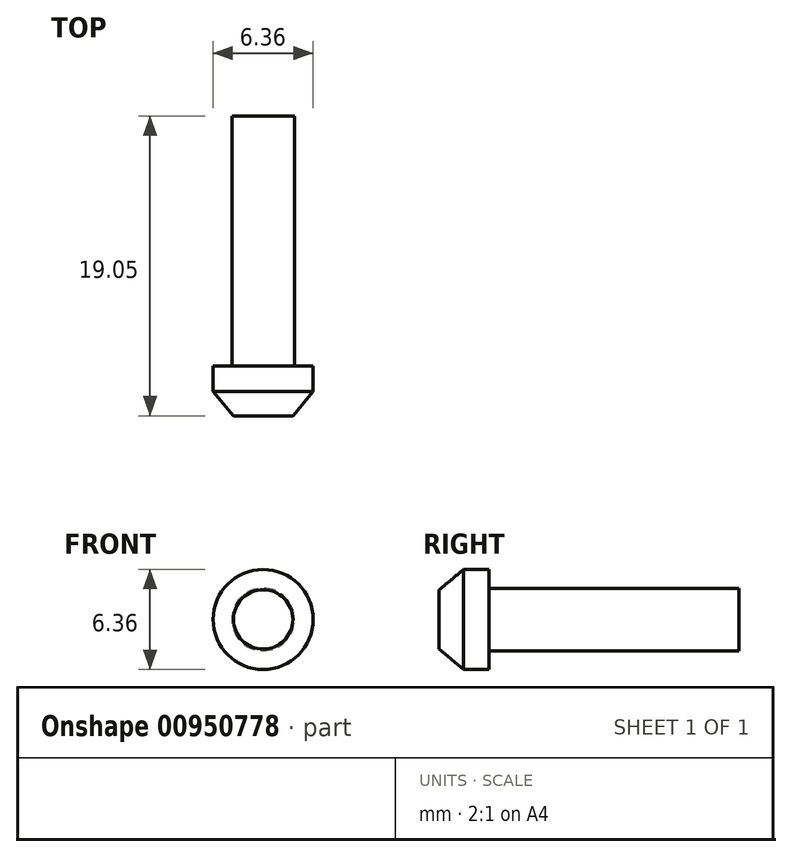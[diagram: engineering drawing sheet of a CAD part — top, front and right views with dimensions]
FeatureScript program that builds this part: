
annotation { "Feature Type Name" : "Feature", "Feature Type Description" : "" }
export const myFeature = defineFeature(function(context is Context, id is Id, definition is map)
    precondition{}
    {
        {
            var Q0;
            Q0=qCreatedBy(makeId("Front.planeOp"),FACE);
            var sketch = newSketch(context, id + "F0", { "sketchPlane" : qUnion([Q0])});
            skLineSegment(sketch, "E0", {"start": v(0, 0) * mm, "end": v(-1.98, 0) * mm});
            skCircle(sketch, "E1", {"center": v(0, 0) * mm, "radius": 1.98 * mm});
            skSolve(sketch);
        }
        {
            var Q0;
            Q0=makeQuery(id+"F0.imprint","IMPRINT",FACE,{"disambiguationData":[TD([[makeQuery(id+"F0.imprint","IMPRINT",EDGE,{"derivedFrom":sQuery(id+"F0.wireOp",EDGE,"E1")}),1.0]])]});
            extrude(context, id + "F1", {"entities" : qUnion([Q0]), "depth" : 15.88 * mm, "offsetDistance" : 25.4 * mm});
        }
        {
            var Q0;
            Q0=makeQuery(id+"F1.opExtrude","CAP_FACE",FACE,{"disambiguationData":[OSD([sQuery(id+"F0.wireOp",EDGE,"E1")])],"isStart":false});
            var sketch = newSketch(context, id + "F2", { "sketchPlane" : qUnion([Q0])});
            skLineSegment(sketch, "E2", {"start": v(0, 0) * mm, "end": v(-3.17, 0) * mm});
            skCircle(sketch, "E3", {"center": v(0, 0) * mm, "radius": 3.17 * mm});
            skSolve(sketch);
        }
        {
            var Q0;
            Q0=makeQuery(id+"F2.imprint","IMPRINT",FACE,{"disambiguationData":[TD([[makeQuery(id+"F2.imprint","IMPRINT",EDGE,{"derivedFrom":sQuery(id+"F2.wireOp",EDGE,"E3")}),1.0]])]});
            var Q1;
            Q1=makeQuery(id+"F2.imprint","IMPRINT",FACE,{"disambiguationData":[TD([[makeQuery(id+"F2.imprint","IMPRINT",EDGE,{"derivedFrom":makeQuery(id+"F1.opExtrude","CAP_EDGE",EDGE,{"disambiguationData":[OSD([sQuery(id+"F0.wireOp",EDGE,"E1")])],"isStart":false})}),1.0]])]});
            extrude(context, id + "F3", {"entities" : qUnion([Q0, Q1]), "operationType" : NewBodyOperationType.ADD, "depth" : 3.17 * mm, "offsetDistance" : 25.4 * mm});
        }
        {
            var Q0;
            Q0=qCreatedBy(makeId("Right.planeOp"),FACE);
            var sketch = newSketch(context, id + "F4", { "sketchPlane" : qUnion([Q0])});
            skLineSegment(sketch, "E4", {"start": v(-16.68, 3.85) * mm, "end": v(-19.86, 1.21) * mm});
            skLineSegment(sketch, "E5", {"start": v(-19.86, 1.21) * mm, "end": v(-19.86, 3.8) * mm});
            skLineSegment(sketch, "E6", {"start": v(-19.86, 3.8) * mm, "end": v(-16.68, 3.85) * mm});
            skLineSegment(sketch, "E7", {"start": v(0, 0) * mm, "end": v(-24.15, 0) * mm});
            skSolve(sketch);
        }
        {
            var Q0;
            Q0=makeQuery(id+"F4.imprint","IMPRINT",FACE,{"disambiguationData":[TD([[makeQuery(id+"F4.imprint","IMPRINT",EDGE,{"derivedFrom":sQuery(id+"F4.wireOp",EDGE,"E4")}),-1.0]])]});
            var Q1;
            Q1=sQuery(id+"F4.wireOp",EDGE,"E7");
            revolve(context, id + "F5", {"operationType" : NewBodyOperationType.REMOVE, "surfaceOperationType" : NewSurfaceOperationType.NEW, "entities" : qUnion([Q0]), "axis" : qUnion([Q1]), "revolveType" : RevolveType.FULL});
        }
    });
